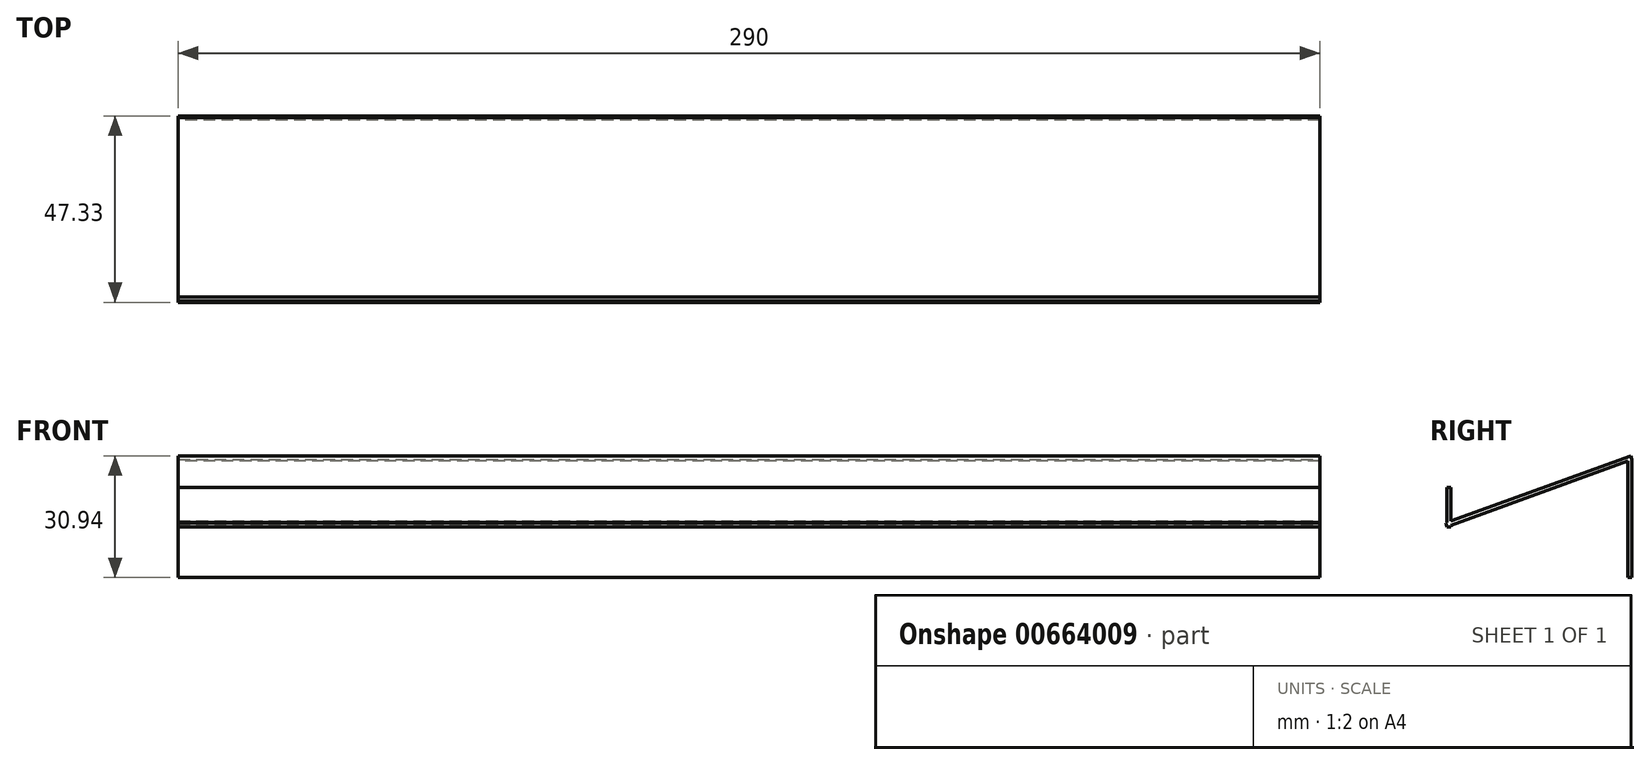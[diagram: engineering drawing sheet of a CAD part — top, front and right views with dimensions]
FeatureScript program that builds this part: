
annotation { "Feature Type Name" : "Feature", "Feature Type Description" : "" }
export const myFeature = defineFeature(function(context is Context, id is Id, definition is map)
    precondition{}
    {
        {
            var Q0;
            Q0=qCreatedBy(makeId("Front.planeOp"),FACE);
            var sketch = newSketch(context, id + "F0", { "sketchPlane" : qUnion([Q0])});
            skLineSegment(sketch, "E0.bottom", {"start": v(0, 0) * mm, "end": v(290, 0) * mm});
            skLineSegment(sketch, "E0.top", {"start": v(0, 30) * mm, "end": v(290, 30) * mm});
            skLineSegment(sketch, "E0.left", {"start": v(0, 0) * mm, "end": v(0, 30) * mm});
            skLineSegment(sketch, "E0.right", {"start": v(290, 0) * mm, "end": v(290, 30) * mm});
            skSolve(sketch);
        }
        {
            var Q0;
            Q0=sQuery(id+"F0.wireOp",EDGE,"E0.top");
            cPlane(context, id + "F1", {"entities" : qUnion([Q0]), "cplaneType" : CPlaneType.LINE_ANGLE, "offset" : 25 * mm, "angle" : 290 * degree, "width" : 150 * mm, "height" : 150 * mm});
        }
        {
            var Q0;
            Q0=qCreatedBy(id+"F1.planeOp",FACE);
            var sketch = newSketch(context, id + "F2", { "sketchPlane" : qUnion([Q0])});
            skLineSegment(sketch, "E1.bottom", {"start": v(0, -10.26) * mm, "end": v(290, -10.26) * mm});
            skLineSegment(sketch, "E1.top", {"start": v(0, 39.74) * mm, "end": v(290, 39.74) * mm});
            skLineSegment(sketch, "E1.left", {"start": v(0, -10.26) * mm, "end": v(0, 39.74) * mm});
            skLineSegment(sketch, "E1.right", {"start": v(290, -10.26) * mm, "end": v(290, 39.74) * mm});
            skSolve(sketch);
        }
        {
            var Q0;
            Q0=sQuery(id+"F0.wireOp",EDGE,"E0.right");
            cPlane(context, id + "F3", {"entities" : qUnion([Q0]), "cplaneType" : CPlaneType.LINE_ANGLE, "offset" : 25 * mm, "angle" : 0 * degree, "width" : 150 * mm, "height" : 150 * mm});
        }
        {
            var Q0;
            Q0=sQuery(id+"F2.wireOp",EDGE,"E1.top");
            cPlane(context, id + "F4", {"entities" : qUnion([Q0]), "cplaneType" : CPlaneType.LINE_ANGLE, "offset" : 25 * mm, "angle" : 0 * degree, "width" : 150 * mm, "height" : 150 * mm});
        }
        {
            var Q0;
            Q0=qCreatedBy(id+"F4.planeOp",FACE);
            var sketch = newSketch(context, id + "F5", { "sketchPlane" : qUnion([Q0])});
            skLineSegment(sketch, "E2.bottom", {"start": v(0, 12.9) * mm, "end": v(-290, 12.9) * mm});
            skLineSegment(sketch, "E2.top", {"start": v(0, 22.9) * mm, "end": v(-290, 22.9) * mm});
            skLineSegment(sketch, "E2.left", {"start": v(0, 12.9) * mm, "end": v(0, 22.9) * mm});
            skLineSegment(sketch, "E2.right", {"start": v(-290, 12.9) * mm, "end": v(-290, 22.9) * mm});
            skSolve(sketch);
        }
        {
            var Q0;
            Q0=makeQuery(id+"F2.imprint","IMPRINT",FACE,{"disambiguationData":[TD([[makeQuery(id+"F2.imprint","IMPRINT",EDGE,{"derivedFrom":sQuery(id+"F2.wireOp",EDGE,"E1.bottom")}),1.0]])]});
            extrude(context, id + "F6", {"entities" : qUnion([Q0]), "oppositeDirection" : true, "depth" : 1 * mm, "offsetDistance" : 25 * mm});
        }
        {
            var Q0;
            Q0=makeQuery(id+"F5.imprint","IMPRINT",FACE,{"disambiguationData":[TD([[makeQuery(id+"F5.imprint","IMPRINT",EDGE,{"derivedFrom":sQuery(id+"F5.wireOp",EDGE,"E2.bottom")}),-1.0]])]});
            extrude(context, id + "F7", {"entities" : qUnion([Q0]), "operationType" : NewBodyOperationType.ADD, "depth" : 1 * mm, "offsetDistance" : 25 * mm});
        }
        {
            var Q0;
            Q0=makeQuery(id+"F0.imprint","IMPRINT",FACE,{"disambiguationData":[TD([[makeQuery(id+"F0.imprint","IMPRINT",EDGE,{"derivedFrom":sQuery(id+"F0.wireOp",EDGE,"E0.bottom")}),1.0]])]});
            extrude(context, id + "F8", {"entities" : qUnion([Q0]), "operationType" : NewBodyOperationType.ADD, "depth" : 1 * mm, "offsetDistance" : 25 * mm});
        }
    });
